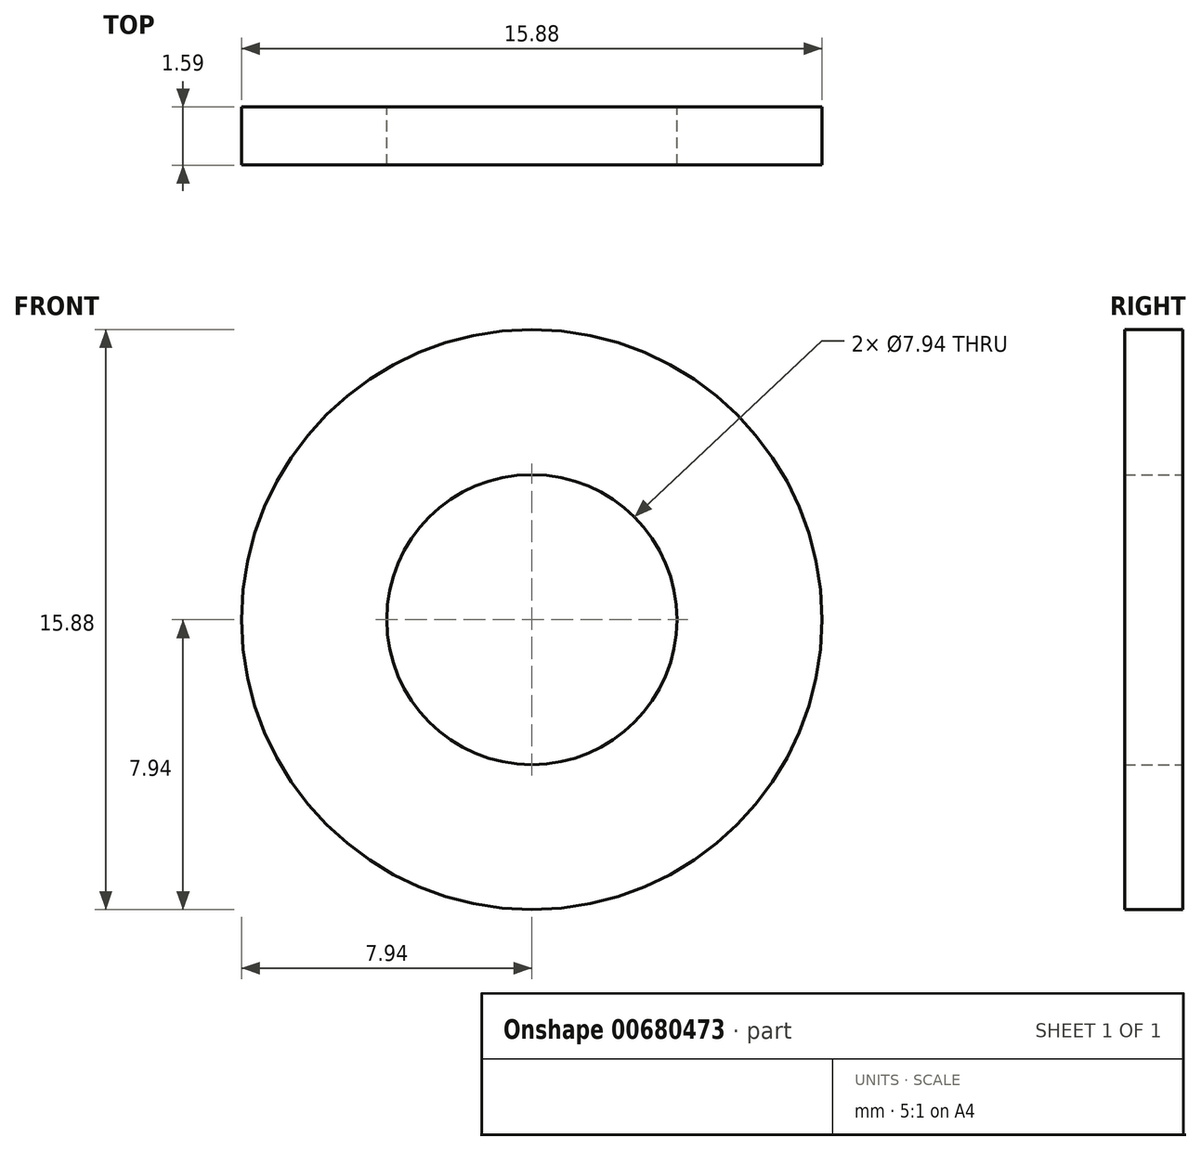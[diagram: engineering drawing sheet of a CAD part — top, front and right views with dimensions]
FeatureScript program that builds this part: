
annotation { "Feature Type Name" : "Feature", "Feature Type Description" : "" }
export const myFeature = defineFeature(function(context is Context, id is Id, definition is map)
    precondition{}
    {
        {
            var Q0;
            Q0=qCreatedBy(makeId("Front.planeOp"),FACE);
            var sketch = newSketch(context, id + "F0", { "sketchPlane" : qUnion([Q0])});
            skCircle(sketch, "E0", {"center": v(0, 0) * mm, "radius": 7.94 * mm});
            skCircle(sketch, "E1", {"center": v(0, 0) * mm, "radius": 3.97 * mm});
            skSolve(sketch);
        }
        {
            var Q0;
            Q0=makeQuery(id+"F0.imprint","IMPRINT",FACE,{"disambiguationData":[TD([[makeQuery(id+"F0.imprint","IMPRINT",EDGE,{"derivedFrom":sQuery(id+"F0.wireOp",EDGE,"E0")}),1.0]])]});
            extrude(context, id + "F1", {"entities" : qUnion([Q0]), "depth" : 1.59 * mm, "offsetDistance" : 25.4 * mm});
        }
    });
